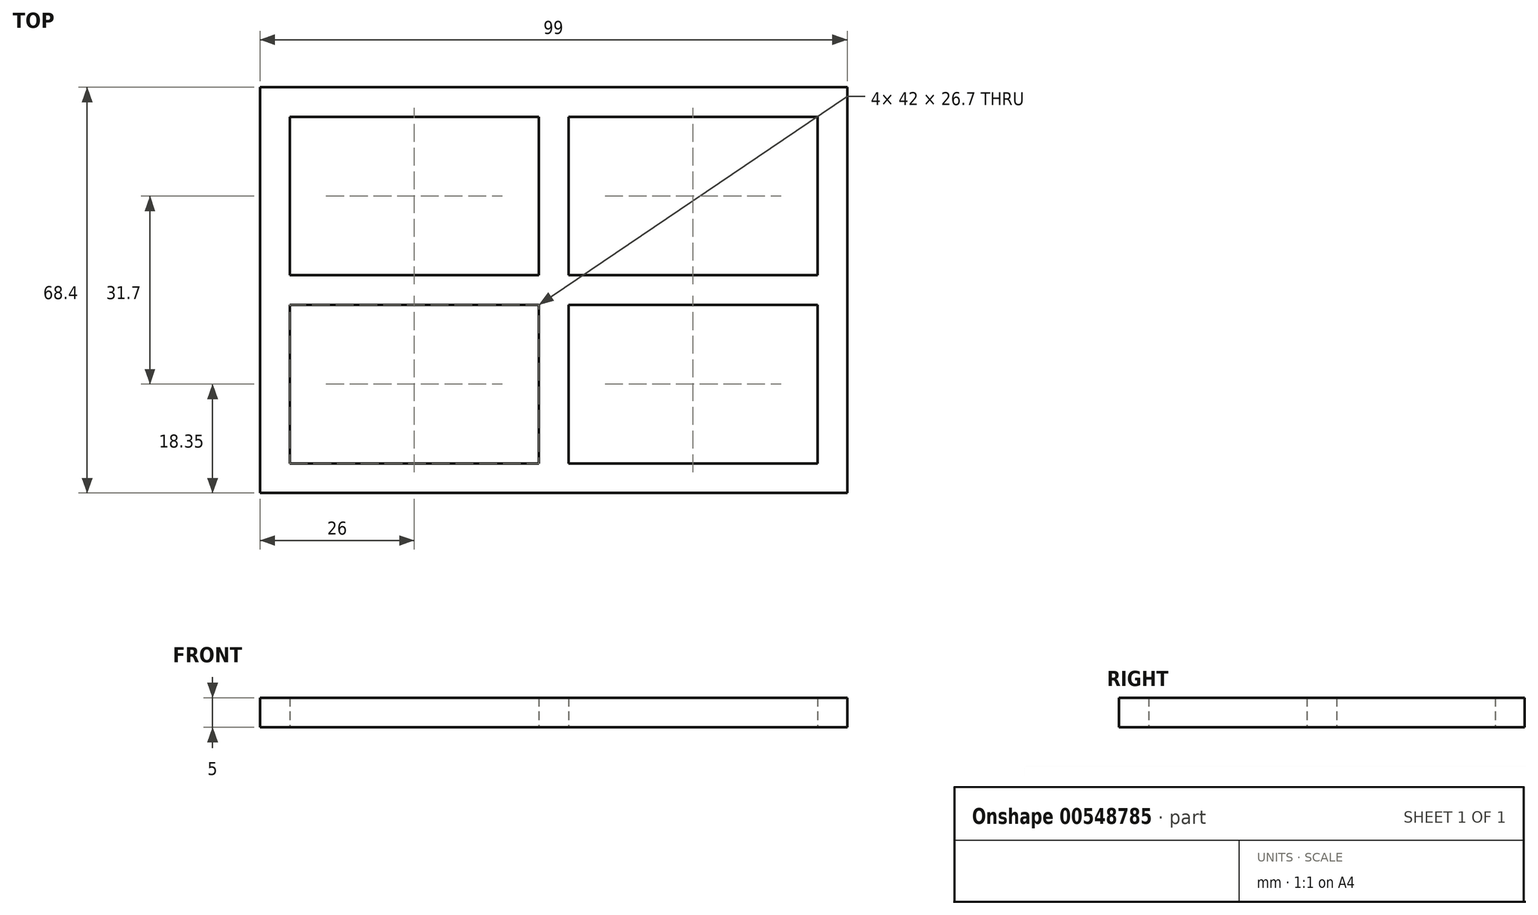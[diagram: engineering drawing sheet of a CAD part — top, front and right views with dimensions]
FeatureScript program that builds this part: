
annotation { "Feature Type Name" : "Feature", "Feature Type Description" : "" }
export const myFeature = defineFeature(function(context is Context, id is Id, definition is map)
    precondition{}
    {
        {
            var Q0;
            Q0=qCreatedBy(makeId("Top.planeOp"),FACE);
            var sketch = newSketch(context, id + "F0", { "sketchPlane" : qUnion([Q0])});
            skLineSegment(sketch, "E0.bottom", {"start": v(49.5, 34.2) * mm, "end": v(-49.5, 34.2) * mm});
            skLineSegment(sketch, "E0.top", {"start": v(49.5, -34.2) * mm, "end": v(-49.5, -34.2) * mm});
            skLineSegment(sketch, "E0.left", {"start": v(49.5, 34.2) * mm, "end": v(49.5, -34.2) * mm});
            skLineSegment(sketch, "E0.right", {"start": v(-49.5, 34.2) * mm, "end": v(-49.5, -34.2) * mm});
            skPoint(sketch, "E0.middle", {"position": v(0, 0) * mm});
            skLineSegment(sketch, "E1.bottom", {"start": v(-44.5, 29.2) * mm, "end": v(-2.5, 29.2) * mm});
            skLineSegment(sketch, "E1.top", {"start": v(-44.5, 2.5) * mm, "end": v(-2.5, 2.5) * mm});
            skLineSegment(sketch, "E1.left", {"start": v(-44.5, 29.2) * mm, "end": v(-44.5, 2.5) * mm});
            skLineSegment(sketch, "E1.right", {"start": v(-2.5, 29.2) * mm, "end": v(-2.5, 2.5) * mm});
            skLineSegment(sketch, "E2.bottom", {"start": v(2.5, 29.2) * mm, "end": v(44.5, 29.2) * mm});
            skLineSegment(sketch, "E2.top", {"start": v(2.5, 2.5) * mm, "end": v(44.5, 2.5) * mm});
            skLineSegment(sketch, "E2.left", {"start": v(2.5, 29.2) * mm, "end": v(2.5, 2.5) * mm});
            skLineSegment(sketch, "E2.right", {"start": v(44.5, 29.2) * mm, "end": v(44.5, 2.5) * mm});
            skLineSegment(sketch, "E3.bottom", {"start": v(44.5, -2.5) * mm, "end": v(2.5, -2.5) * mm});
            skLineSegment(sketch, "E3.top", {"start": v(44.5, -29.2) * mm, "end": v(2.5, -29.2) * mm});
            skLineSegment(sketch, "E3.left", {"start": v(44.5, -2.5) * mm, "end": v(44.5, -29.2) * mm});
            skLineSegment(sketch, "E3.right", {"start": v(2.5, -2.5) * mm, "end": v(2.5, -29.2) * mm});
            skLineSegment(sketch, "E4.bottom", {"start": v(-2.5, -2.5) * mm, "end": v(-44.5, -2.5) * mm});
            skLineSegment(sketch, "E4.top", {"start": v(-2.5, -29.2) * mm, "end": v(-44.5, -29.2) * mm});
            skLineSegment(sketch, "E4.left", {"start": v(-2.5, -2.5) * mm, "end": v(-2.5, -29.2) * mm});
            skLineSegment(sketch, "E4.right", {"start": v(-44.5, -2.5) * mm, "end": v(-44.5, -29.2) * mm});
            skSolve(sketch);
        }
        {
            var Q0;
            Q0 = qSketchRegion(id + "F0", true);
            extrude(context, id + "F1", {"entities" : qUnion([Q0]), "depth" : 5 * mm, "offsetDistance" : 25 * mm});
        }
    });
